# Revit family: Domotics-DomesticRanges-GEWISS-CHORUS_COMMAND-PUSH-BUTTON_2M
name_source: partatom
category: Apparecchi elettrici
revit_build: Autodesk Revit 2016 (Build: 20161004_0715(x64)
units: mm (PartAtom-declared; Revit-internal decimal feet)

## family parameters
Condiviso = Sì
Host = Superficie
Mantenere orientamento annotazione = Sì
Numero OmniClass = 23.80.50.11.14
Punto di calcolo locali = Sì
Quota connettore circolare = Usa diametro
Taglio con vuoti quando caricato = Sì
Tipo di parte = Normale
Titolo OmniClass = Switches

## types (9) — shared parameters
Bidimensionale = bidimensionale pulsanti 2m : GW10173
Breaking capacity: = 1.25 In (200 position changes)
Catalogue = DOMOTICS
Catalogue Range = CHORUS - DOMESTIC RANGE
Category = Push-button
Electrocod = 0130
Glow Wire Test = 850°C
IDF = f8531931-b237-4683-81e0-b3baab97f80c
IDT = af1ad8d5-3b0e-403c-83b9-0b1d0abc0b2f
Immagine tipo = GW14173.jpg
Insulation resistance = > 5 MOhm
Larghezza pulsante = 46 mm  [stored 0.150919 ft]
No. Chorus modules = 2
Number of poles = 1P
Produttore = GEWISS S.p.A.
Prolonged operation (no.of position changes) = 40.000 at In 250 V ac cosÃ˜=0,6
Prospetto di default = 1219 mm
Resistance at test voltage = 2000 V at 50 Hz for 1 minute
SEO = Push button
Simbolo_ = SIMBOLO PULSANTI : LUM
Standard; = EN 60669-1
Technical sheet = https://www.gewiss.com
Terminal grip on cable traction = > 50 N
Terminal tightening capacity flexible cables (mm2) = min. 0,75 - max. 2x4
Terminal tightening capacity rigid cables (mm2) = min. 0,5 - max. 2x2,5
Thermo-pressure with ball = 125
Tipo_ = CHORUS PULSANTI 2M_BASE : GW14173 - Titanio - Illuminabile segnalazione
URL = https://www.gewiss.com
Version file RFA = 19.0
Voltage = 250 V ac
Voltage: = 250 V ac
Wiring terminals = With screw

## per-type parameters (varying)
| type | Button key | Colour | Description: | Descrizione | EAN code | Modello | Type |
| GW14171 - Titanium | Neutral | Titanium | 1P NO - 16A | PUSH-BUTTON 2M 1P NO 16A TITANIUM | 8011564266032 | GW14171 | General |
| GW14172 - Titanium - Illuminable | With diffuser | Titanium | 1P NO - 16A illuminable | P-BUTTON 2M 1P NO 16A ILL LOC TITANIUM | 8011564266056 | GW14172 | Backlit |
| GW12171 - Black | Neutral | Black | 1P NO - 16A | PUSH-BUTTON 2M 1P NO 16A BLACK | 8011564269439 | GW12171 | General |
| GW10173 - White - Illuminable | With replaceable neutral lens | White | 1P NO - 16A illuminable | PUSH-BUTTON, 2M 1P NO 16A ILL SIG WHITE | 8011564258631 | GW10173 | Indicator |
| GW12173 - Black - Illuminable | With replaceable neutral lens | Black | 1P NO - 16A illuminable | PUSH-BUTTON 2M 1P NO 16A ILL SIG BLACK | 8011564269477 | GW12173 | Indicator |
| GW14173 - Titanium - Illuminable | With replaceable neutral lens | Titanium | 1P NO - 16A illuminable | P-BUTTON 2M 1P NO 16A ILL SIG TITANIUM | 8011564266070 | GW14173 | Indicator |
| GW10172 - White - Illuminable | With diffuser | White | 1P NO - 16A illuminable | PUSH-BUTTON, 2M 1P NO 16A ILL LOC WHITE | 8011564258617 | GW10172 | Backlit |
| GW10171 - White | Neutral | White | 1P NO - 16A | PUSH-BUTTON, 2M 1P NO 16A WHITE | 8011564258594 | GW10171 | General |
| GW12172 - Black - Illuminable | With diffuser | Black | 1P NO - 16A illuminable | PUSH-BUTTON 2M 1P NO 16A ILL LOC BLACK | 8011564269453 | GW12172 | Backlit |

note: source unit labels omitted for Thermo-pressure with ball — the stored unit's dimension contradicts the parameter name (converter mislabeling)

note: [stored X ft] marks values corroborated as IEEE doubles in the binary element streams (Revit-internal decimal feet)

## geometry (parser evidence)
native form markers: Sweep x1
no freeform markers — native parametric forms only
